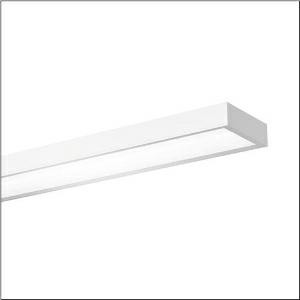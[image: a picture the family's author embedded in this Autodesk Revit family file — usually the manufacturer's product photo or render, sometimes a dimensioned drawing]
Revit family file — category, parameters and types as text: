
# Revit family: sport_31_51hs12dc4dca
name_source: partatom
category: Lighting Fixtures
units: mm (PartAtom-declared; Revit-internal decimal feet)

## family parameters
Cut with Voids When Loaded = No
Host = Face
Light Source = No
Part Type = Normal
Room Calculation Point = No
Round Connector Dimension = Use Diameter
Shared = No

## types (1)
- --- (1 x LED, 8000 lm, 59.4 W, 4000K)
    Apparent Load = 59 VA
    CIE Flux Codes = 65 89 97 100 100
    Color Rendering = 80
    Color Temperature = 4000K
    Default Elevation = 1800 mm
    Description = Sport 31, high bay luminaire, primary light control with reflector, of sheet steel, primary anti-glare with prismatic structure, of PC, primary optical cover: cover panel, of PC, light emission: direct distribution, primary light characteristic: symmetric, installation type: suspended mounting, recessed, surface-mounted, LED, rated luminous flux: 8.000lm, luminous efficacy: 135lm/W, light colour: 840, colour temperature: 4000K, control gear: DALI 2, with terminal, 5-pole, max. 2.5mm², mains connection: 220..240V, AC/DC, 50/60Hz, rated input power: 58W, housing, of sheet steel, traffic white (RAL 9016), length: 1.540mm, width: 315mm, height: 95mm, protection rating (complete): IP20, protection rating (lamp compartment, on room side): IP50, insulation class (complete): insulation class I (protective earthing), certification: CE, ENEC, UKCA, ball protection: ball impact resistant with ceiling mounting or chain suspension, impact resistance: IK08, permissible operating ambient temperature: -20..+35°C, standard: DIN 18032-3, EN 60598-2-22, packaging unit: 1 piece
    Height = 100 mm  [stored 0.328084 ft]
    Lamp = 1 x LED
    Lamp Light Flux = 8000 lm
    Lamp Power = 59.4 W
    Lamp count = 1
    Length = 1500 mm
    Luminous efficacy = 135 lm/W
    Manufacturer = Siteco
    ModVariant = No
    Model = 51HS12DC4DCA
    Mounting Place = Ceiling
    Mounting Type = Pendant
    Number of Poles = 1
    OnlyDefault = Yes
    Power Factor = 1
    Product Name = Sport 31
    Product group = high bay luminaire
    ProductGroupID = 901
    Protection Class = Protection class I
    Protection Degree = IP 20
    RLX_Detail_Level = 1
    RLX_Emergency_Light_Flux = 0 lm
    RLX_Emergency_Type = 0
    RLX_Emergency_Type_DB = No
    RlxData = <blob elided: 22773 chars, md5=bf19f099>
    Socket = socket
    Standby Power = 0 W
    System Light Flux = 8000 lm
    System Power = 59 W
    Type Comments = factory setting: luminous flux: 100 % | dim-lin: 254 | 247 mA
    Type Image = l_1006823.jpg
    URL = http://relux.com
    VarID = @adj_218519
    Voltage = 0 V
    Weight = 0.00 kg
    Width = 315 mm

note: [stored X ft] marks values corroborated as IEEE doubles in the binary element streams (Revit-internal decimal feet)

## geometry (parser evidence)
native form markers: Blend x4, Sweep x11
no freeform markers — native parametric forms only
